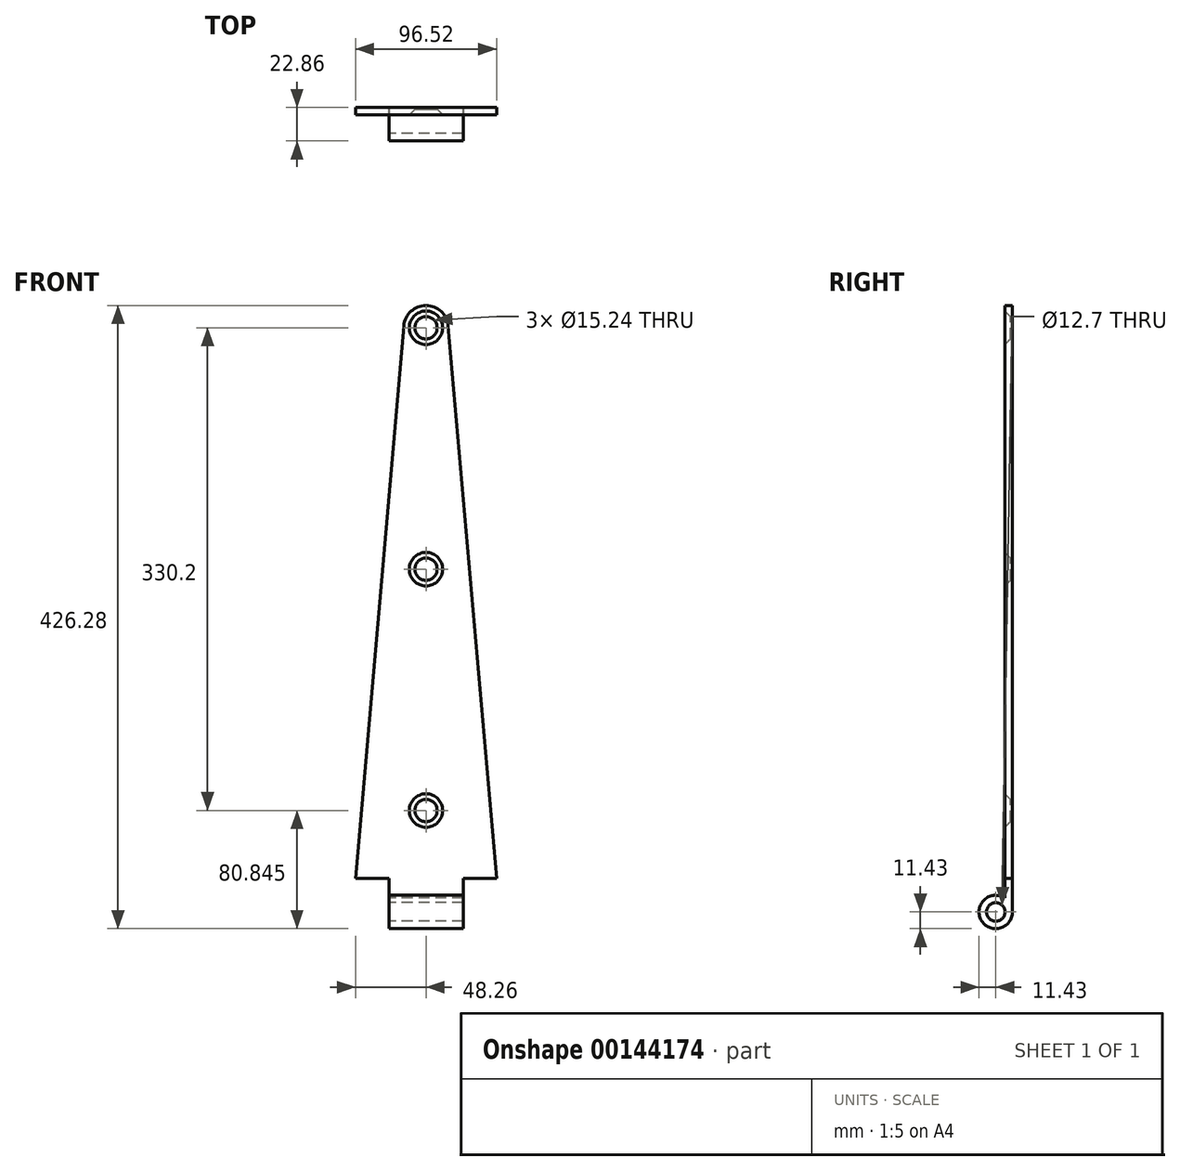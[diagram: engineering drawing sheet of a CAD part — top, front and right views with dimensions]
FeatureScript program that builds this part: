
annotation { "Feature Type Name" : "Feature", "Feature Type Description" : "" }
export const myFeature = defineFeature(function(context is Context, id is Id, definition is map)
    precondition{}
    {
        {
            var Q0;
            Q0=qCreatedBy(makeId("Front.planeOp"),FACE);
            var sketch = newSketch(context, id + "F0", { "sketchPlane" : qUnion([Q0])});
            skLineSegment(sketch, "E0", {"start": v(0, 0) * mm, "end": v(96.52, 0) * mm});
            skLineSegment(sketch, "E1", {"start": v(0, 0) * mm, "end": v(48.26, 551.61) * mm});
            skLineSegment(sketch, "E2", {"start": v(96.52, 0) * mm, "end": v(48.26, 551.61) * mm});
            skSolve(sketch);
        }
        {
            var Q0;
            Q0=makeQuery(id+"F0.imprint","IMPRINT",FACE,{"disambiguationData":[TD([[makeQuery(id+"F0.imprint","IMPRINT",EDGE,{"derivedFrom":sQuery(id+"F0.wireOp",EDGE,"E0")}),1.0]])]});
            extrude(context, id + "F1", {"entities" : qUnion([Q0]), "depth" : 5.08 * mm});
        }
        {
            var Q0;
            Q0=makeQuery(id+"F1.opExtrude","SWEPT_FACE",FACE,{"disambiguationData":[OSD([sQuery(id+"F0.wireOp",EDGE,"E0")])]});
            var sketch = newSketch(context, id + "F2", { "sketchPlane" : qUnion([Q0])});
            skLineSegment(sketch, "E3", {"start": v(0, 5.08) * mm, "end": v(22.86, 5.08) * mm, "construction": true});
            skLineSegment(sketch, "E4", {"start": v(96.52, 5.08) * mm, "end": v(73.66, 5.08) * mm, "construction": true});
            skLineSegment(sketch, "E5.bottom", {"start": v(22.86, 5.08) * mm, "end": v(73.66, 5.08) * mm});
            skLineSegment(sketch, "E5.top", {"start": v(22.86, 0) * mm, "end": v(73.66, 0) * mm});
            skLineSegment(sketch, "E5.left", {"start": v(22.86, 5.08) * mm, "end": v(22.86, 0) * mm});
            skLineSegment(sketch, "E5.right", {"start": v(73.66, 5.08) * mm, "end": v(73.66, 0) * mm});
            skSolve(sketch);
        }
        {
            var Q0;
            Q0=makeQuery(id+"F2.imprint","IMPRINT",FACE,{"disambiguationData":[TD([[makeQuery(id+"F2.imprint","IMPRINT",EDGE,{"derivedFrom":sQuery(id+"F2.wireOp",EDGE,"E5.bottom")}),-1.0]])]});
            extrude(context, id + "F3", {"entities" : qUnion([Q0]), "operationType" : NewBodyOperationType.ADD, "depth" : 22.86 * mm});
        }
        {
            var Q0;
            Q0=makeQuery(id+"F3.opExtrude","CAP_FACE",FACE,{"disambiguationData":[OSD([sQuery(id+"F2.wireOp",EDGE,"E5.bottom"),sQuery(id+"F2.wireOp",EDGE,"E5.top"),sQuery(id+"F2.wireOp",EDGE,"E5.left"),sQuery(id+"F2.wireOp",EDGE,"E5.right")])],"isStart":false});
            var sketch = newSketch(context, id + "F4", { "sketchPlane" : qUnion([Q0])});
            skLineSegment(sketch, "E6", {"start": v(22.86, 5.08) * mm, "end": v(22.86, 11.43) * mm});
            skLineSegment(sketch, "E7", {"start": v(22.86, 11.43) * mm, "end": v(48.26, 11.43) * mm});
            skSolve(sketch);
        }
        {
            var Q0;
            Q0=makeQuery(id+"F4.imprint","IMPRINT",FACE,{"disambiguationData":[TD([[makeQuery(id+"F4.imprint","IMPRINT",EDGE,{"derivedFrom":makeQuery(id+"F3.opExtrude","CAP_EDGE",EDGE,{"disambiguationData":[OSD([sQuery(id+"F2.wireOp",EDGE,"E5.bottom")])],"isStart":false})}),-1.0]])]});
            var Q1;
            Q1=sQuery(id+"F4.wireOp",EDGE,"E7");
            revolve(context, id + "F5", {"operationType" : NewBodyOperationType.ADD, "entities" : qUnion([Q0]), "axis" : qUnion([Q1]), "revolveType" : RevolveType.FULL});
        }
        {
            var Q0;
            Q0=makeQuery(id+"F1.opExtrude","SWEPT_EDGE",EDGE,{"disambiguationData":[OSD([sQuery(id+"F0.wireOp",EDGE,"E1"),sQuery(id+"F0.wireOp",EDGE,"E2")])]});
            fillet(context, id + "F6", {"entities" : qUnion([Q0]), "radius" : 15.24 * mm, "tangentPropagation" : true, "allowEdgeOverflow" : false});
        }
        {
            var Q0;
            Q0=makeQuery(id+"F3.boolean.opBoolean","MERGE",FACE,{"derivedFrom":[makeQuery(id+"F1.opExtrude","CAP_FACE",FACE,{"disambiguationData":[OSD([sQuery(id+"F0.wireOp",EDGE,"E0"),sQuery(id+"F0.wireOp",EDGE,"E1"),sQuery(id+"F0.wireOp",EDGE,"E2")])],"isStart":false}),makeQuery(id+"F3.opExtrude","SWEPT_FACE",FACE,{"disambiguationData":[OSD([sQuery(id+"F2.wireOp",EDGE,"E5.bottom")])]})]});
            var sketch = newSketch(context, id + "F7", { "sketchPlane" : qUnion([Q0])});
            skPoint(sketch, "E8", {"position": v(48.26, 376.75) * mm});
            skPoint(sketch, "E9", {"position": v(48.26, 211.65) * mm});
            skPoint(sketch, "E10", {"position": v(48.26, 46.55) * mm});
            skSolve(sketch);
        }
        {
            var Q0;
            Q0=sQuery(id+"F7.wireOp",VERTEX,"E10");
            var Q1;
            Q1=sQuery(id+"F7.wireOp",VERTEX,"E9");
            var Q2;
            Q2=sQuery(id+"F7.wireOp",VERTEX,"E8");
            var Q3;
            Q3=makeQuery(id+"F1.opExtrude","SWEPT_BODY",BODY,{"disambiguationData":[OSD([sQuery(id+"F0.wireOp",EDGE,"E0"),sQuery(id+"F0.wireOp",EDGE,"E1"),sQuery(id+"F0.wireOp",EDGE,"E2")])]});
            hole(context, id + "F8", {"style" : HoleStyle.C_SINK, "endStyle" : HoleEndStyle.THROUGH, "holeDiameter" : 15.24 * mm, "cSinkDiameter" : 22.86 * mm, "cSinkAngle" : 90 * degree, "locations" : qUnion([Q0, Q1, Q2]), "scope" : qUnion([Q3]), "isTappedThrough" : true});
        }
    });
